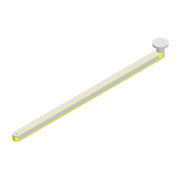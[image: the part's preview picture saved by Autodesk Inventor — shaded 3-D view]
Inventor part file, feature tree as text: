
AUTODESK INVENTOR PART (.ipt)
format: ipt  version: 2022 (Build 260153000, 153)  size: 112,128 bytes
history: native  units: mm
features: sketch x4, extrude x3, projected_geometry x2
ambient origin geometry x8: Origin, YZ Plane, XZ Plane, XY Plane, X Axis, Y Axis, Z Axis, Center Point
bodies: Solid1 (feature_tree)
feature tree (9):
  extrude  "Extrusion1"  Depth=10.0mm
  extrude  "Extrusion2"  Depth=3.0mm
  sketch  "Sketch3"  dims[d4=8.0mm d5=0.0mm d12=10.0mm]
  extrude  "Extrusion3"  Depth=10.0mm
  sketch  "Sketch1"  dims[d0=244.795mm d1=10.0mm]
  sketch  "Sketch2"  dims[d2=3.0mm d3=3.0mm]
  projected_geometry  "Projected Loop1"
  projected_geometry  "Projected Loop2"
  sketch  "Sketch4"  dims[d13=12.0mm d14=0.0mm d15=20.0mm d16=3.0mm d17=0.0mm]
